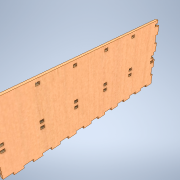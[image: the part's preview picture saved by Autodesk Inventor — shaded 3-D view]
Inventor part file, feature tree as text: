
AUTODESK INVENTOR PART (.ipt)
format: ipt  version: 2021 (Build 250183000, 183)  size: 315,392 bytes
history: native  units: mm
features: extrude x4, sketch x4, other x1
ambient origin geometry x8: Origin, YZ Plane, XZ Plane, XY Plane, X Axis, Y Axis, Z Axis, Center Point
bodies: Solid1 (feature_tree)
feature tree (9):
  other  "DoosjeRechter-Linkerkant"
  extrude  "Extrusion1"  Depth=200.0mm
  extrude  "Extrusion2"  Depth=100.0mm
  extrude  "Extrusion3"  Depth=3.0mm TaperAngle=0.0deg
  extrude  "Extrusion4"  Depth=3.0mm TaperAngle=0.0deg
  sketch  "Sketch1"  dims[d0=77.0mm d1=200.0mm]
  sketch  "Sketch2"  dims[d2=3.0mm d3=0.0mm d7=100.0mm d9=20.0mm d10=10.0mm d12=10.0mm]
  sketch  "Sketch3"  dims[d25=10.0mm d26=3.0mm d27=0.0mm]
  sketch  "Sketch4"  dims[d28=10.0mm d29=3.0mm d30=10.0mm d31=20.0mm d32=3.0mm d33=0.0mm d34=4.0mm d35=3.0mm d36=60.0mm d38=38.0mm d39=20.0mm d41=38.0mm d44=0.0mm d45=0.0mm d46=60.0mm d48=38.0mm d49=20.0mm d51=6.5mm d54=3.5mm d55=3.5mm]
